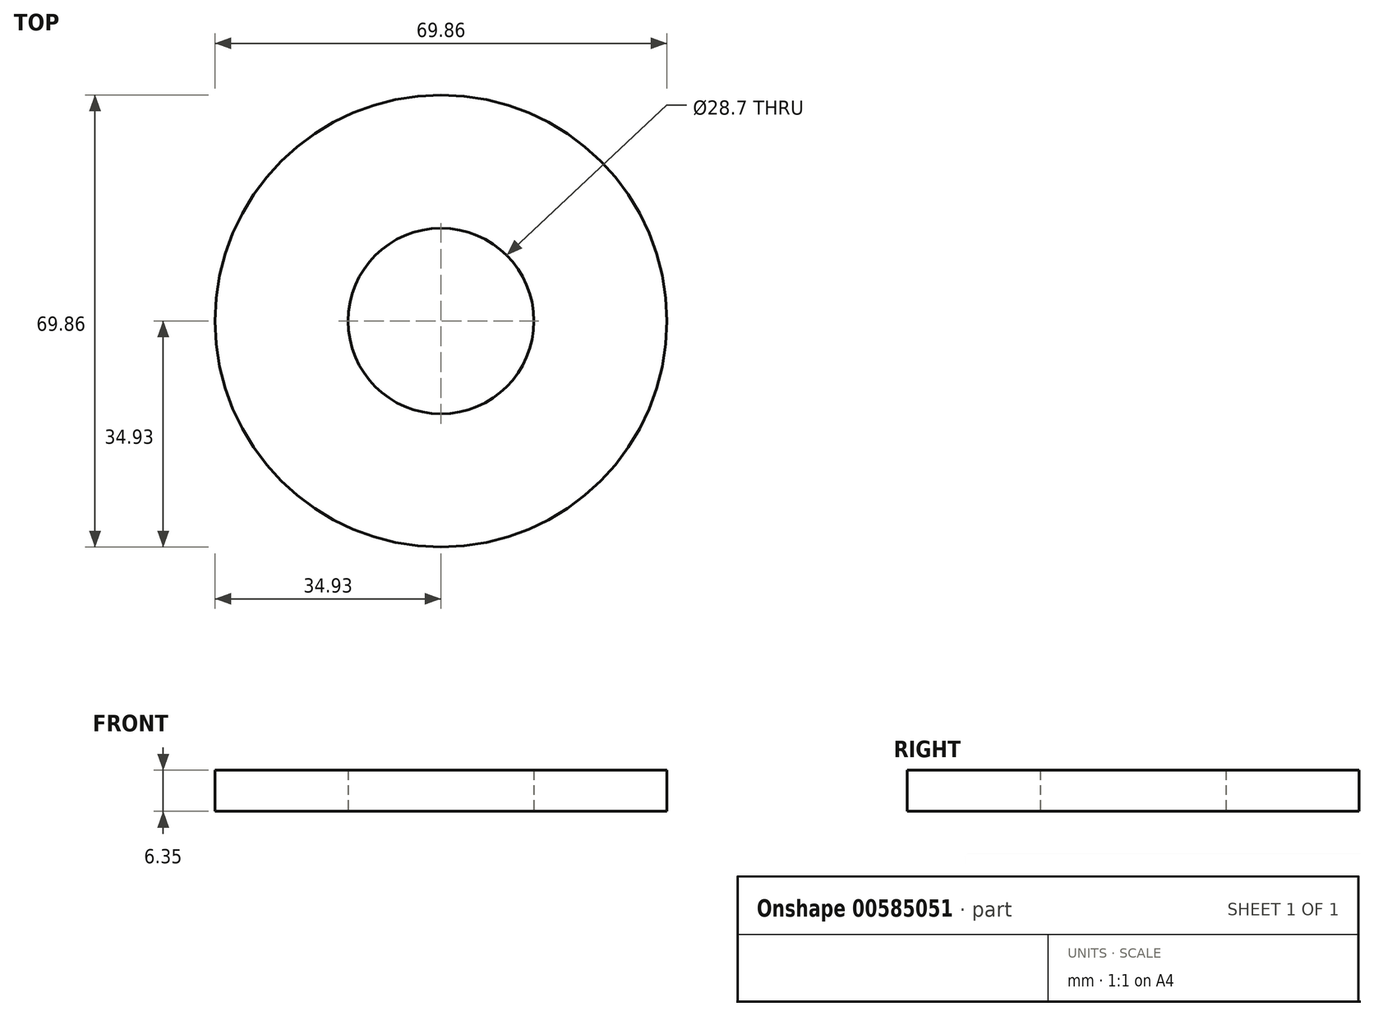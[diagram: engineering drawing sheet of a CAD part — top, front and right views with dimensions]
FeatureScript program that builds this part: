
annotation { "Feature Type Name" : "Feature", "Feature Type Description" : "" }
export const myFeature = defineFeature(function(context is Context, id is Id, definition is map)
    precondition{}
    {
        {
            var Q0;
            Q0=qCreatedBy(makeId("Top.planeOp"),FACE);
            var sketch = newSketch(context, id + "F0", { "sketchPlane" : qUnion([Q0])});
            skCircle(sketch, "E0.cCircle", {"center": v(0, 0) * mm, "radius": 22.23 * mm, "construction": true});
            skLineSegment(sketch, "E0.0", {"start": v(22.23, 12.83) * mm, "end": v(22.23, -12.83) * mm, "construction": true});
            skLineSegment(sketch, "E0.1", {"start": v(22.23, -12.83) * mm, "end": v(0, -25.66) * mm});
            skLineSegment(sketch, "E0.2", {"start": v(0, -25.66) * mm, "end": v(-22.22, -12.83) * mm});
            skLineSegment(sketch, "E0.3", {"start": v(-22.22, -12.83) * mm, "end": v(-22.23, 12.83) * mm});
            skLineSegment(sketch, "E0.4", {"start": v(-22.23, 12.83) * mm, "end": v(0, 25.66) * mm});
            skLineSegment(sketch, "E0.5", {"start": v(0, 25.66) * mm, "end": v(22.23, 12.83) * mm});
            skPoint(sketch, "E0.0.midPoint", {"position": v(22.23, 0) * mm});
            skCircle(sketch, "E1", {"center": v(0, 0) * mm, "radius": 34.93 * mm});
            skCircle(sketch, "E2", {"center": v(0, 0) * mm, "radius": 14.35 * mm});
            skSolve(sketch);
        }
        {
            var Q0;
            Q0 = qSketchRegion(id + "F0", true);
            extrude(context, id + "F1", {"entities" : qUnion([Q0]), "depth" : 6.35 * mm, "offsetDistance" : 25.4 * mm});
        }
    });
